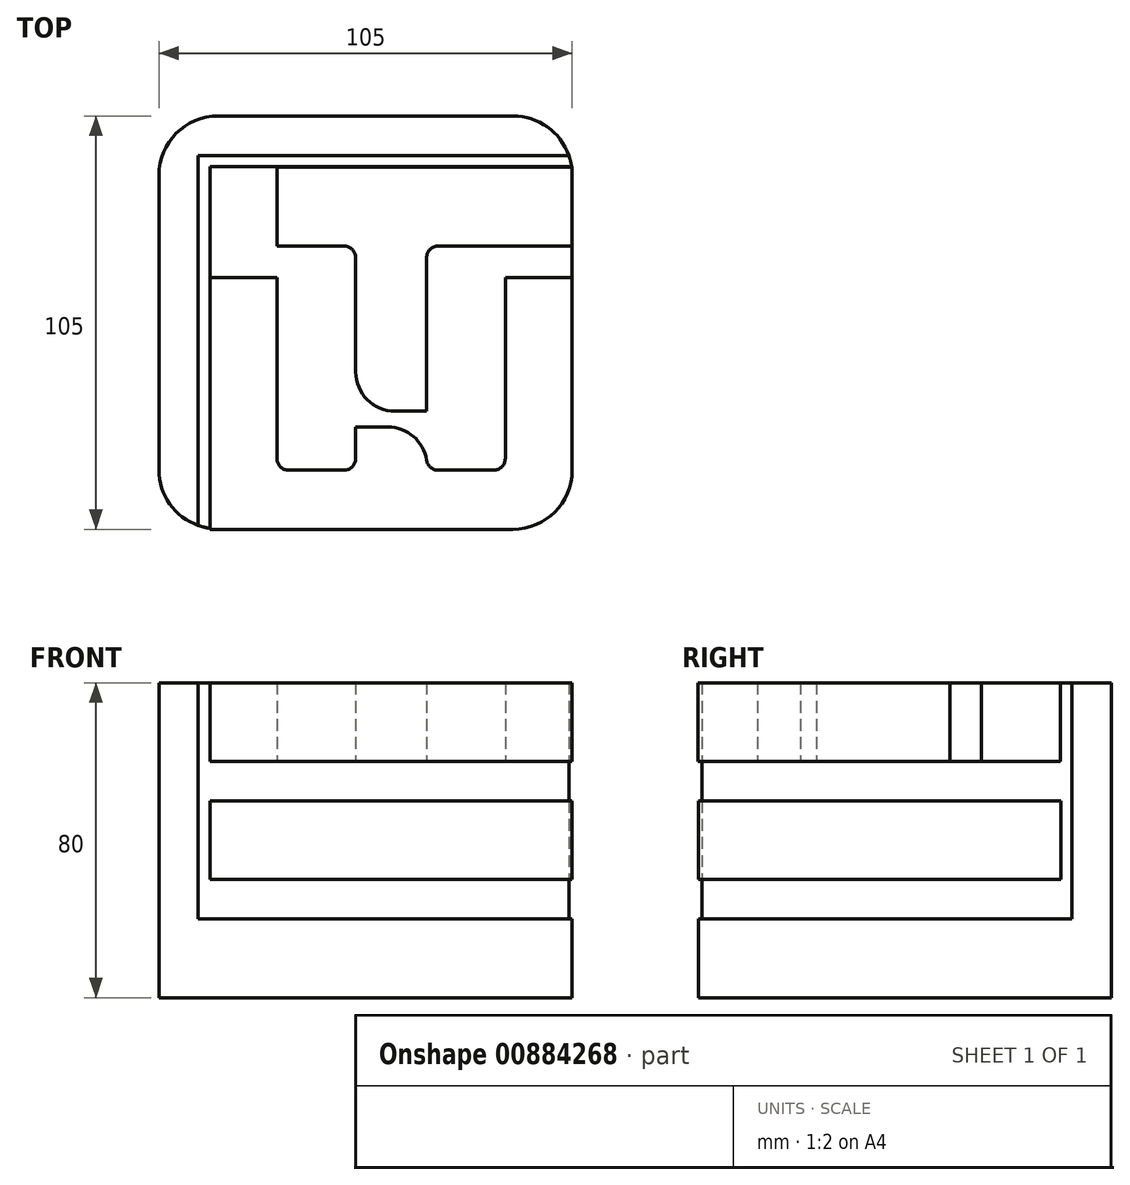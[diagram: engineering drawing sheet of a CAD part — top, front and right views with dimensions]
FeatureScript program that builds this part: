
annotation { "Feature Type Name" : "Feature", "Feature Type Description" : "" }
export const myFeature = defineFeature(function(context is Context, id is Id, definition is map)
    precondition{}
    {
        {
            var Q0;
            Q0=qCreatedBy(makeId("Top.planeOp"),FACE);
            var sketch = newSketch(context, id + "F0", { "sketchPlane" : qUnion([Q0])});
            skLineSegment(sketch, "E0.bottom", {"start": v(50, -50) * mm, "end": v(-50, -50) * mm});
            skLineSegment(sketch, "E0.top", {"start": v(50, 50) * mm, "end": v(-50, 50) * mm});
            skLineSegment(sketch, "E0.left", {"start": v(50, -50) * mm, "end": v(50, 50) * mm});
            skLineSegment(sketch, "E0.right", {"start": v(-50, -50) * mm, "end": v(-50, 50) * mm});
            skPoint(sketch, "E0.middle", {"position": v(0, 0) * mm});
            skLineSegment(sketch, "E1", {"start": v(45, 19) * mm, "end": v(28, 19) * mm});
            skLineSegment(sketch, "E2", {"start": v(28, 19) * mm, "end": v(28, -30) * mm});
            skLineSegment(sketch, "E3", {"start": v(28, -30) * mm, "end": v(8, -30) * mm});
            skLineSegment(sketch, "E4", {"start": v(8, -30) * mm, "end": v(8, 27) * mm});
            skLineSegment(sketch, "E5", {"start": v(8, 27) * mm, "end": v(45, 27) * mm});
            skLineSegment(sketch, "E6", {"start": v(45, 27) * mm, "end": v(45, 47) * mm});
            skLineSegment(sketch, "E7", {"start": v(45, 47) * mm, "end": v(-47, 47) * mm});
            skLineSegment(sketch, "E8", {"start": v(-47, 47) * mm, "end": v(-47, 27) * mm});
            skLineSegment(sketch, "E9", {"start": v(-47, 27) * mm, "end": v(-10, 27) * mm});
            skLineSegment(sketch, "E10", {"start": v(-10, 27) * mm, "end": v(-10, -30) * mm});
            skLineSegment(sketch, "E11", {"start": v(-10, -30) * mm, "end": v(-30, -30) * mm});
            skLineSegment(sketch, "E12", {"start": v(-30, -30) * mm, "end": v(-30, 47) * mm});
            skLineSegment(sketch, "E13", {"start": v(-30, 47) * mm, "end": v(-47, 47) * mm});
            skLineSegment(sketch, "E14", {"start": v(-47, 47) * mm, "end": v(-47, -45) * mm});
            skLineSegment(sketch, "E15", {"start": v(-47, -45) * mm, "end": v(45, -45) * mm});
            skLineSegment(sketch, "E16", {"start": v(45, -45) * mm, "end": v(45, 19) * mm});
            skLineSegment(sketch, "E17.bottom", {"start": v(60, -60) * mm, "end": v(-60, -60) * mm});
            skLineSegment(sketch, "E17.top", {"start": v(60, 60) * mm, "end": v(-60, 60) * mm});
            skLineSegment(sketch, "E17.left", {"start": v(60, -60) * mm, "end": v(60, 60) * mm});
            skLineSegment(sketch, "E17.right", {"start": v(-60, -60) * mm, "end": v(-60, 60) * mm});
            skLineSegment(sketch, "E18.bottom", {"start": v(-22, -22.5) * mm, "end": v(-14.5, -22.5) * mm});
            skLineSegment(sketch, "E18.top", {"start": v(-22, 22.5) * mm, "end": v(-14.5, 22.5) * mm});
            skLineSegment(sketch, "E18.left", {"start": v(-22, -22.5) * mm, "end": v(-22, 22.5) * mm});
            skLineSegment(sketch, "E18.right", {"start": v(-14.5, -22.5) * mm, "end": v(-14.5, 22.5) * mm});
            skPoint(sketch, "E18.middle", {"position": v(-18.25, 0) * mm});
            skLineSegment(sketch, "E19.bottom", {"start": v(14.5, -22.5) * mm, "end": v(22, -22.5) * mm});
            skLineSegment(sketch, "E19.top", {"start": v(14.5, 22.5) * mm, "end": v(22, 22.5) * mm});
            skLineSegment(sketch, "E19.left", {"start": v(14.5, -22.5) * mm, "end": v(14.5, 22.5) * mm});
            skLineSegment(sketch, "E19.right", {"start": v(22, -22.5) * mm, "end": v(22, 22.5) * mm});
            skPoint(sketch, "E19.middle", {"position": v(18.25, 0) * mm});
            skLineSegment(sketch, "E20", {"start": v(-30, 19) * mm, "end": v(-47, 19) * mm});
            skLineSegment(sketch, "E21.bottom", {"start": v(-10, -19) * mm, "end": v(8, -19) * mm});
            skLineSegment(sketch, "E21.top", {"start": v(-10, -15) * mm, "end": v(8, -15) * mm});
            skLineSegment(sketch, "E21.left", {"start": v(-10, -19) * mm, "end": v(-10, -15) * mm});
            skLineSegment(sketch, "E21.right", {"start": v(8, -19) * mm, "end": v(8, -15) * mm});
            skSolve(sketch);
        }
        {
            var Q0;
            Q0=makeQuery(id+"F0.imprint","IMPRINT",FACE,{"disambiguationData":[TD([[makeQuery(id+"F0.imprint","IMPRINT",EDGE,{"derivedFrom":sQuery(id+"F0.wireOp",EDGE,"E1")}),1.0]])]});
            var Q1;
            {var subQ5=sQuery(id+"F0.wireOp",EDGE,"E13");Q1=makeQuery(id+"F0.imprint","IMPRINT",FACE,{"disambiguationData":[TD([[makeQuery(id+"F0.imprint","IMPRINT",EDGE,{"derivedFrom":subQ5}),1.0]])]});}
            var Q2;
            {var subQ1=sQuery(id+"F0.wireOp",EDGE,"E5");Q2=makeQuery(id+"F0.imprint","IMPRINT",FACE,{"disambiguationData":[TD([[makeQuery(id+"F0.imprint","IMPRINT",EDGE,{"derivedFrom":subQ1}),1.0]])]});}
            extrude(context, id + "F1", {"entities" : qUnion([Q0, Q1, Q2]), "depth" : 10 * mm, "offsetDistance" : 25 * mm, "hasSecondDirection" : true, "secondDirectionOppositeDirection" : true, "secondDirectionDepth" : 10 * mm});
        }
        {
            var Q0;
            Q0=qCreatedBy(makeId("Top.planeOp"),FACE);
            cPlane(context, id + "F2", {"entities" : qUnion([Q0]), "cplaneType" : CPlaneType.OFFSET, "offset" : 30 * mm, "oppositeDirection" : true, "width" : 150 * mm, "height" : 150 * mm});
        }
        {
            var Q0;
            Q0=qCreatedBy(makeId("Top.planeOp"),FACE);
            cPlane(context, id + "F3", {"entities" : qUnion([Q0]), "cplaneType" : CPlaneType.OFFSET, "offset" : 60 * mm, "oppositeDirection" : true, "width" : 150 * mm, "height" : 150 * mm});
        }
        {
            var Q0;
            Q0=qCreatedBy(makeId("Top.planeOp"),FACE);
            var sketch = newSketch(context, id + "F4", { "sketchPlane" : qUnion([Q0])});
            skLineSegment(sketch, "E22", {"start": v(-50, -44.89) * mm, "end": v(-60, -44.89) * mm});
            skLineSegment(sketch, "E23", {"start": v(-60, -44.89) * mm, "end": v(-60, 60) * mm});
            skLineSegment(sketch, "E24", {"start": v(-60, 60) * mm, "end": v(45, 60) * mm});
            skLineSegment(sketch, "E25", {"start": v(45, 60) * mm, "end": v(45, 50) * mm});
            skLineSegment(sketch, "E26", {"start": v(45, 50) * mm, "end": v(-50, 50) * mm});
            skLineSegment(sketch, "E27", {"start": v(-50, 50) * mm, "end": v(-50, -44.89) * mm});
            skSolve(sketch);
        }
        {
            var Q0;
            Q0=makeQuery(id+"F4.imprint","IMPRINT",FACE,{"disambiguationData":[TD([[makeQuery(id+"F4.imprint","IMPRINT",EDGE,{"derivedFrom":sQuery(id+"F4.wireOp",EDGE,"E22")}),-1.0]])]});
            extrude(context, id + "F5", {"entities" : qUnion([Q0]), "depth" : 10 * mm, "offsetDistance" : 25 * mm, "hasSecondDirection" : true, "secondDirectionOppositeDirection" : true, "secondDirectionDepth" : 70 * mm});
        }
        {
            var Q0;
            Q0=qCreatedBy(id+"F3.planeOp",FACE);
            var sketch = newSketch(context, id + "F6", { "sketchPlane" : qUnion([Q0])});
            skLineSegment(sketch, "E28.bottom", {"start": v(-60, -44.89) * mm, "end": v(45, -44.89) * mm});
            skLineSegment(sketch, "E28.top", {"start": v(-60, 60) * mm, "end": v(45, 60) * mm});
            skLineSegment(sketch, "E28.left", {"start": v(-60, -44.89) * mm, "end": v(-60, 60) * mm});
            skLineSegment(sketch, "E28.right", {"start": v(45, -44.89) * mm, "end": v(45, 60) * mm});
            skSolve(sketch);
        }
        {
            var Q0;
            Q0 = qSketchRegion(id + "F6", true);
            extrude(context, id + "F7", {"entities" : qUnion([Q0]), "operationType" : NewBodyOperationType.ADD, "endBound" : BoundingType.SYMMETRIC, "depth" : 20 * mm, "offsetDistance" : 25 * mm});
        }
        {
            var Q0;
            Q0=qCreatedBy(id+"F2.planeOp",FACE);
            var sketch = newSketch(context, id + "F8", { "sketchPlane" : qUnion([Q0])});
            skLineSegment(sketch, "E29.top", {"start": v(-47, 47.11) * mm, "end": v(45, 47.11) * mm});
            skLineSegment(sketch, "E29.left", {"start": v(-47, -44.89) * mm, "end": v(-47, 47.11) * mm});
            skLineSegment(sketch, "E29.right", {"start": v(45, -44.89) * mm, "end": v(45, 47.11) * mm});
            skLineSegment(sketch, "E30", {"start": v(-47, -44.89) * mm, "end": v(45, -44.89) * mm});
            skSolve(sketch);
        }
        {
            var Q0;
            Q0 = qSketchRegion(id + "F8", true);
            extrude(context, id + "F9", {"entities" : qUnion([Q0]), "endBound" : BoundingType.SYMMETRIC, "depth" : 20 * mm, "offsetDistance" : 25 * mm});
        }
        {
            var Q0;
            Q0=makeQuery(id+"F5.opExtrude","SWEPT_EDGE",EDGE,{"disambiguationData":[OSD([sQuery(id+"F4.wireOp",EDGE,"E24"),sQuery(id+"F4.wireOp",EDGE,"E25")])]});
            var Q1;
            Q1=makeQuery(id+"F5.opExtrude","SWEPT_EDGE",EDGE,{"disambiguationData":[OSD([sQuery(id+"F4.wireOp",EDGE,"E22"),sQuery(id+"F4.wireOp",EDGE,"E23")])]});
            var Q2;
            Q2=makeQuery(id+"F7.opExtrude","SWEPT_EDGE",EDGE,{"disambiguationData":[OSD([sQuery(id+"F6.wireOp",EDGE,"E28.bottom"),sQuery(id+"F6.wireOp",EDGE,"E28.right")])]});
            var Q3;
            Q3=makeQuery(id+"F1.opExtrude","SWEPT_EDGE",EDGE,{"disambiguationData":[OSD([sQuery(id+"F0.wireOp",EDGE,"E15"),sQuery(id+"F0.wireOp",EDGE,"E16")])]});
            var Q4;
            Q4=makeQuery(id+"F5.opExtrude","SWEPT_EDGE",EDGE,{"disambiguationData":[OSD([sQuery(id+"F4.wireOp",EDGE,"E23"),sQuery(id+"F4.wireOp",EDGE,"E24")])]});
            var Q5;
            Q5=makeQuery(id+"F9.opExtrude","SWEPT_EDGE",EDGE,{"disambiguationData":[OSD([sQuery(id+"F8.wireOp",EDGE,"E29.right"),sQuery(id+"F8.wireOp",EDGE,"E30")])]});
            fillet(context, id + "F10", {"entities" : qUnion([Q0, Q1, Q2, Q3, Q4, Q5]), "radius" : 15 * mm, "tangentPropagation" : true, "allowEdgeOverflow" : false});
        }
        {
            var Q0;
            Q0=makeQuery(id+"F1.opExtrude","SWEPT_EDGE",EDGE,{"disambiguationData":[OSD([sQuery(id+"F0.wireOp",EDGE,"E3"),sQuery(id+"F0.wireOp",EDGE,"E4")])]});
            var Q1;
            Q1=makeQuery(id+"F1.opExtrude","SWEPT_EDGE",EDGE,{"disambiguationData":[OSD([sQuery(id+"F0.wireOp",EDGE,"E11"),sQuery(id+"F0.wireOp",EDGE,"E12")])]});
            var Q2;
            Q2=makeQuery(id+"F1.opExtrude","SWEPT_EDGE",EDGE,{"disambiguationData":[OSD([sQuery(id+"F0.wireOp",EDGE,"E10"),sQuery(id+"F0.wireOp",EDGE,"E11")])]});
            var Q3;
            Q3=makeQuery(id+"F1.opExtrude","SWEPT_EDGE",EDGE,{"disambiguationData":[OSD([sQuery(id+"F0.wireOp",EDGE,"E2"),sQuery(id+"F0.wireOp",EDGE,"E3")])]});
            var Q4;
            Q4=makeQuery(id+"F1.opExtrude","SWEPT_EDGE",EDGE,{"disambiguationData":[OSD([sQuery(id+"F0.wireOp",EDGE,"E9"),sQuery(id+"F0.wireOp",EDGE,"E10")])]});
            var Q5;
            Q5=makeQuery(id+"F1.opExtrude","SWEPT_EDGE",EDGE,{"disambiguationData":[OSD([sQuery(id+"F0.wireOp",EDGE,"E4"),sQuery(id+"F0.wireOp",EDGE,"E5")])]});
            fillet(context, id + "F11", {"entities" : qUnion([Q0, Q1, Q2, Q3, Q4, Q5]), "radius" : 3 * mm, "tangentPropagation" : true, "allowEdgeOverflow" : false});
        }
        {
            var Q0;
            Q0=makeQuery(id+"F1.opExtrude","SWEPT_EDGE",EDGE,{"disambiguationData":[OSD([sQuery(id+"F0.wireOp",EDGE,"E10"),sQuery(id+"F0.wireOp",EDGE,"E21.top"),sQuery(id+"F0.wireOp",EDGE,"E21.left")])]});
            var Q1;
            Q1=makeQuery(id+"F1.opExtrude","SWEPT_EDGE",EDGE,{"disambiguationData":[OSD([sQuery(id+"F0.wireOp",EDGE,"E4"),sQuery(id+"F0.wireOp",EDGE,"E21.bottom"),sQuery(id+"F0.wireOp",EDGE,"E21.right")])]});
            fillet(context, id + "F12", {"entities" : qUnion([Q0, Q1]), "radius" : 10 * mm, "tangentPropagation" : true, "allowEdgeOverflow" : false});
        }
    });
